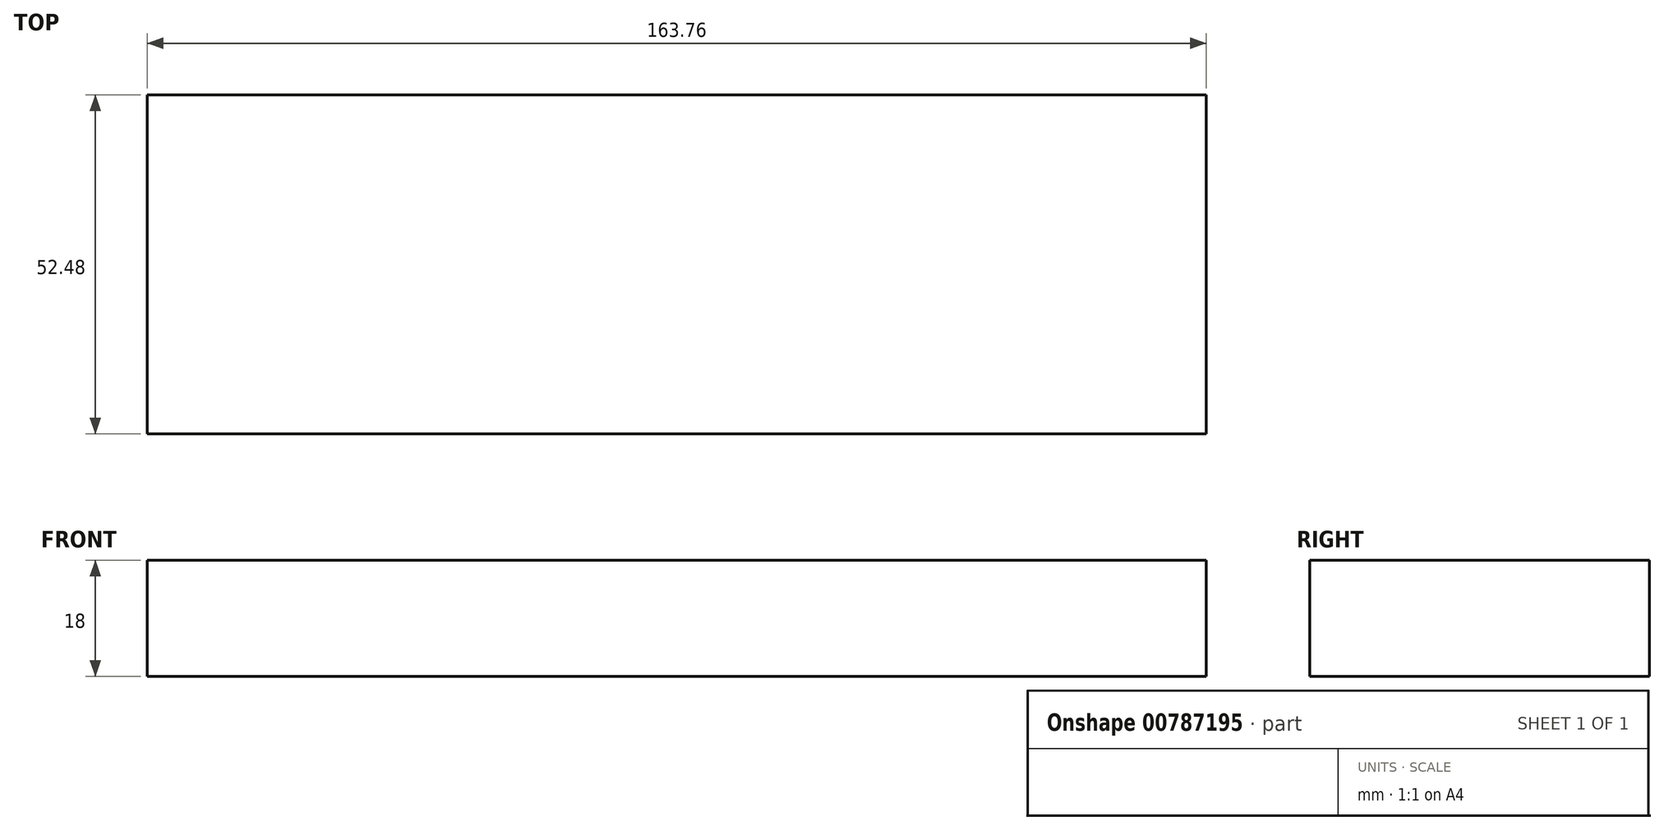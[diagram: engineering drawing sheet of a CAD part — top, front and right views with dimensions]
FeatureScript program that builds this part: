
annotation { "Feature Type Name" : "Feature", "Feature Type Description" : "" }
export const myFeature = defineFeature(function(context is Context, id is Id, definition is map)
    precondition{}
    {
        {
            var Q0;
            Q0=qCreatedBy(makeId("Top.planeOp"),FACE);
            var sketch = newSketch(context, id + "F0", { "sketchPlane" : qUnion([Q0])});
            skLineSegment(sketch, "E0.bottom", {"start": v(-107.42, 33.9) * mm, "end": v(56.34, 33.9) * mm});
            skLineSegment(sketch, "E0.top", {"start": v(-107.42, -18.57) * mm, "end": v(56.34, -18.57) * mm});
            skLineSegment(sketch, "E0.left", {"start": v(-107.42, 33.9) * mm, "end": v(-107.42, -18.57) * mm});
            skLineSegment(sketch, "E0.right", {"start": v(56.34, 33.9) * mm, "end": v(56.34, -18.57) * mm});
            skSolve(sketch);
        }
        {
            var Q0;
            Q0=makeQuery(id+"F0.imprint","IMPRINT",FACE,{"disambiguationData":[TD([[makeQuery(id+"F0.imprint","IMPRINT",EDGE,{"derivedFrom":sQuery(id+"F0.wireOp",EDGE,"E0.bottom")}),-1.0]])]});
            extrude(context, id + "F1", {"entities" : qUnion([Q0]), "depth" : 18 * mm, "offsetDistance" : 25.4 * mm});
        }
    });
